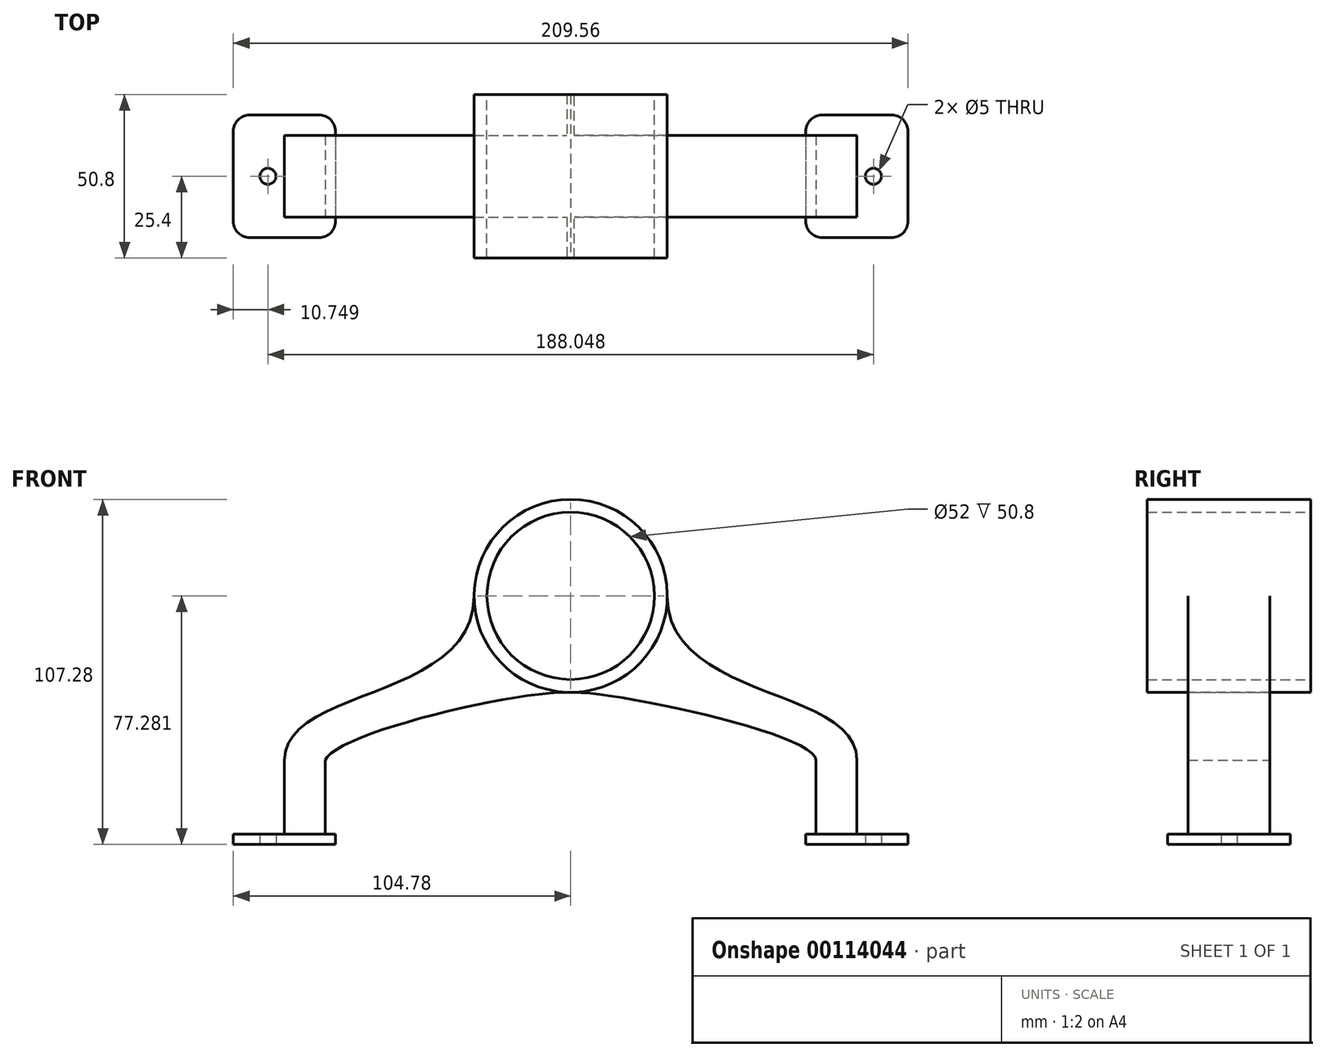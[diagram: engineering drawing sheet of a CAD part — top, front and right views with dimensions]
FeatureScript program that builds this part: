
annotation { "Feature Type Name" : "Feature", "Feature Type Description" : "" }
export const myFeature = defineFeature(function(context is Context, id is Id, definition is map)
    precondition{}
    {
        {
            var Q0;
            Q0=qCreatedBy(makeId("Front.planeOp"),FACE);
            var sketch = newSketch(context, id + "F0", { "sketchPlane" : qUnion([Q0])});
            skCircle(sketch, "E0", {"center": v(0, 51.11) * mm, "radius": 26 * mm});
            skCircle(sketch, "E1", {"center": v(0, 51.11) * mm, "radius": 30 * mm});
            skFitSpline(sketch, "E2", {"points": [v(-30, 51.11) * mm, v(-88.9, 0) * mm], "startDerivative": vector(0, -97.77) * mm, "endDerivative": vector(0, -68.8) * mm});
            skFitSpline(sketch, "E3", {"points": [v(30, 51.11) * mm, v(88.9, 0) * mm], "startDerivative": vector(0, -97.77) * mm, "endDerivative": vector(0, -68.8) * mm});
            skLineSegment(sketch, "E4", {"start": v(-88.9, 0) * mm, "end": v(-88.9, -26.17) * mm});
            skLineSegment(sketch, "E5", {"start": v(-88.9, -26.17) * mm, "end": v(-76.2, -26.17) * mm});
            skLineSegment(sketch, "E6", {"start": v(-76.2, -26.17) * mm, "end": v(-76.2, 0) * mm});
            skLineSegment(sketch, "E7", {"start": v(88.9, 0) * mm, "end": v(88.9, -26.17) * mm});
            skLineSegment(sketch, "E8", {"start": v(88.9, -26.17) * mm, "end": v(76.2, -26.17) * mm});
            skLineSegment(sketch, "E9", {"start": v(76.2, -26.17) * mm, "end": v(76.2, 0) * mm});
            skFitSpline(sketch, "E10", {"points": [v(-76.2, 0) * mm, v(0, 21.11) * mm], "startDerivative": vector(8.17, 24.91) * mm, "endDerivative": vector(51.52, -1.87) * mm});
            skFitSpline(sketch, "E11", {"points": [v(76.2, 0) * mm, v(0, 21.11) * mm], "startDerivative": vector(0, 24.91) * mm, "endDerivative": vector(-37.71, -1.87) * mm});
            skSolve(sketch);
        }
        {
            var Q0;
            Q0=makeQuery(id+"F0.imprint","IMPRINT",FACE,{"disambiguationData":[TD([[makeQuery(id+"F0.imprint","IMPRINT",EDGE,{"derivedFrom":sQuery(id+"F0.wireOp",EDGE,"E0")}),-1.0]])]});
            extrude(context, id + "F1", {"entities" : qUnion([Q0]), "endBound" : BoundingType.SYMMETRIC, "depth" : 50.8 * mm});
        }
        {
            var Q0;
            {var subQ0=sQuery(id+"F0.wireOp",EDGE,"E2");Q0=makeQuery(id+"F0.imprint","IMPRINT",FACE,{"disambiguationData":[TD([[makeQuery(id+"F0.imprint","IMPRINT",EDGE,{"derivedFrom":subQ0}),1.0]])]});}
            var Q1;
            {var subQ0=sQuery(id+"F0.wireOp",EDGE,"E3");Q1=makeQuery(id+"F0.imprint","IMPRINT",FACE,{"disambiguationData":[TD([[makeQuery(id+"F0.imprint","IMPRINT",EDGE,{"derivedFrom":subQ0}),-1.0]])]});}
            extrude(context, id + "F2", {"entities" : qUnion([Q0, Q1]), "operationType" : NewBodyOperationType.ADD, "endBound" : BoundingType.SYMMETRIC, "depth" : 25.4 * mm});
        }
        {
            var Q0;
            Q0=makeQuery(id+"F2.opExtrude","SWEPT_FACE",FACE,{"disambiguationData":[OSD([sQuery(id+"F0.wireOp",EDGE,"E5")])]});
            var sketch = newSketch(context, id + "F3", { "sketchPlane" : qUnion([Q0])});
            skPoint(sketch, "E12.middle", {"position": v(-88.9, 0) * mm});
            skLineSegment(sketch, "E13", {"start": v(0, -42.78) * mm, "end": v(0, 35) * mm, "construction": true});
            skLineSegment(sketch, "E14.bottom", {"start": v(-73.03, -19.05) * mm, "end": v(-104.78, -19.05) * mm});
            skLineSegment(sketch, "E14.top", {"start": v(-73.03, 19.05) * mm, "end": v(-104.78, 19.05) * mm});
            skLineSegment(sketch, "E14.left", {"start": v(-73.03, -19.05) * mm, "end": v(-73.03, 19.05) * mm});
            skLineSegment(sketch, "E14.right", {"start": v(-104.78, -19.05) * mm, "end": v(-104.78, 19.05) * mm});
            skLineSegment(sketch, "E15.MirrorCS", {"start": v(73.03, -19.05) * mm, "end": v(104.78, -19.05) * mm});
            skLineSegment(sketch, "E16.MirrorCS", {"start": v(104.78, -19.05) * mm, "end": v(104.78, 19.05) * mm});
            skLineSegment(sketch, "E17.MirrorCS", {"start": v(73.03, -19.05) * mm, "end": v(73.03, 19.05) * mm});
            skLineSegment(sketch, "E18.MirrorCS", {"start": v(73.03, 19.05) * mm, "end": v(104.78, 19.05) * mm});
            skSolve(sketch);
        }
        {
            var Q0;
            Q0 = qSketchRegion(id + "F3", true);
            extrude(context, id + "F4", {"entities" : qUnion([Q0]), "operationType" : NewBodyOperationType.ADD, "oppositeDirection" : true, "depth" : 3.17 * mm});
        }
        {
            var Q0;
            Q0=makeQuery(id+"F4.opExtrude","SWEPT_EDGE",EDGE,{"disambiguationData":[OSD([sQuery(id+"F3.wireOp",EDGE,"E14.top"),sQuery(id+"F3.wireOp",EDGE,"E14.right")])]});
            var Q1;
            Q1=makeQuery(id+"F4.opExtrude","SWEPT_EDGE",EDGE,{"disambiguationData":[OSD([sQuery(id+"F3.wireOp",EDGE,"E14.top"),sQuery(id+"F3.wireOp",EDGE,"E14.left")])]});
            var Q2;
            Q2=makeQuery(id+"F4.opExtrude","SWEPT_EDGE",EDGE,{"disambiguationData":[OSD([sQuery(id+"F3.wireOp",EDGE,"E14.bottom"),sQuery(id+"F3.wireOp",EDGE,"E14.right")])]});
            var Q3;
            Q3=makeQuery(id+"F4.opExtrude","SWEPT_EDGE",EDGE,{"disambiguationData":[OSD([sQuery(id+"F3.wireOp",EDGE,"E14.bottom"),sQuery(id+"F3.wireOp",EDGE,"E14.left")])]});
            fillet(context, id + "F5", {"entities" : qUnion([Q0, Q1, Q2, Q3]), "radius" : 5.08 * mm, "tangentPropagation" : true, "allowEdgeOverflow" : false});
        }
        {
            var Q0;
            Q0=makeQuery(id+"F4.opExtrude","SWEPT_EDGE",EDGE,{"disambiguationData":[OSD([sQuery(id+"F3.wireOp",EDGE,"E16.MirrorCS"),sQuery(id+"F3.wireOp",EDGE,"E18.MirrorCS")])]});
            var Q1;
            Q1=makeQuery(id+"F4.opExtrude","SWEPT_EDGE",EDGE,{"disambiguationData":[OSD([sQuery(id+"F3.wireOp",EDGE,"E17.MirrorCS"),sQuery(id+"F3.wireOp",EDGE,"E18.MirrorCS")])]});
            var Q2;
            Q2=makeQuery(id+"F4.opExtrude","SWEPT_EDGE",EDGE,{"disambiguationData":[OSD([sQuery(id+"F3.wireOp",EDGE,"E15.MirrorCS"),sQuery(id+"F3.wireOp",EDGE,"E16.MirrorCS")])]});
            var Q3;
            Q3=makeQuery(id+"F4.opExtrude","SWEPT_EDGE",EDGE,{"disambiguationData":[OSD([sQuery(id+"F3.wireOp",EDGE,"E15.MirrorCS"),sQuery(id+"F3.wireOp",EDGE,"E17.MirrorCS")])]});
            fillet(context, id + "F6", {"entities" : qUnion([Q0, Q1, Q2, Q3]), "radius" : 5.08 * mm, "tangentPropagation" : true, "allowEdgeOverflow" : false});
        }
        {
            var Q0;
            Q0=makeQuery(id+"F4.boolean.opBoolean","MERGE",FACE,{"derivedFrom":[makeQuery(id+"F2.opExtrude","SWEPT_FACE",FACE,{"disambiguationData":[OSD([sQuery(id+"F0.wireOp",EDGE,"E5")])]}),makeQuery(id+"F4.opExtrude","CAP_FACE",FACE,{"disambiguationData":[OSD([sQuery(id+"F3.wireOp",EDGE,"E14.bottom"),sQuery(id+"F3.wireOp",EDGE,"E14.top"),sQuery(id+"F3.wireOp",EDGE,"E14.left"),sQuery(id+"F3.wireOp",EDGE,"E14.right")])],"isStart":true})]});
            var sketch = newSketch(context, id + "F7", { "sketchPlane" : qUnion([Q0])});
            skCircle(sketch, "E19", {"center": v(-94.03, 0) * mm, "radius": 2.5 * mm});
            skPoint(sketch, "E19.centerSnap0", {"position": v(-104.78, 0) * mm});
            skCircle(sketch, "E20", {"center": v(94.02, 0) * mm, "radius": 2.5 * mm});
            skSolve(sketch);
        }
        {
            var Q0;
            Q0 = qSketchRegion(id + "F7", true);
            extrude(context, id + "F8", {"entities" : qUnion([Q0]), "operationType" : NewBodyOperationType.REMOVE, "oppositeDirection" : true, "depth" : 25.4 * mm});
        }
    });
